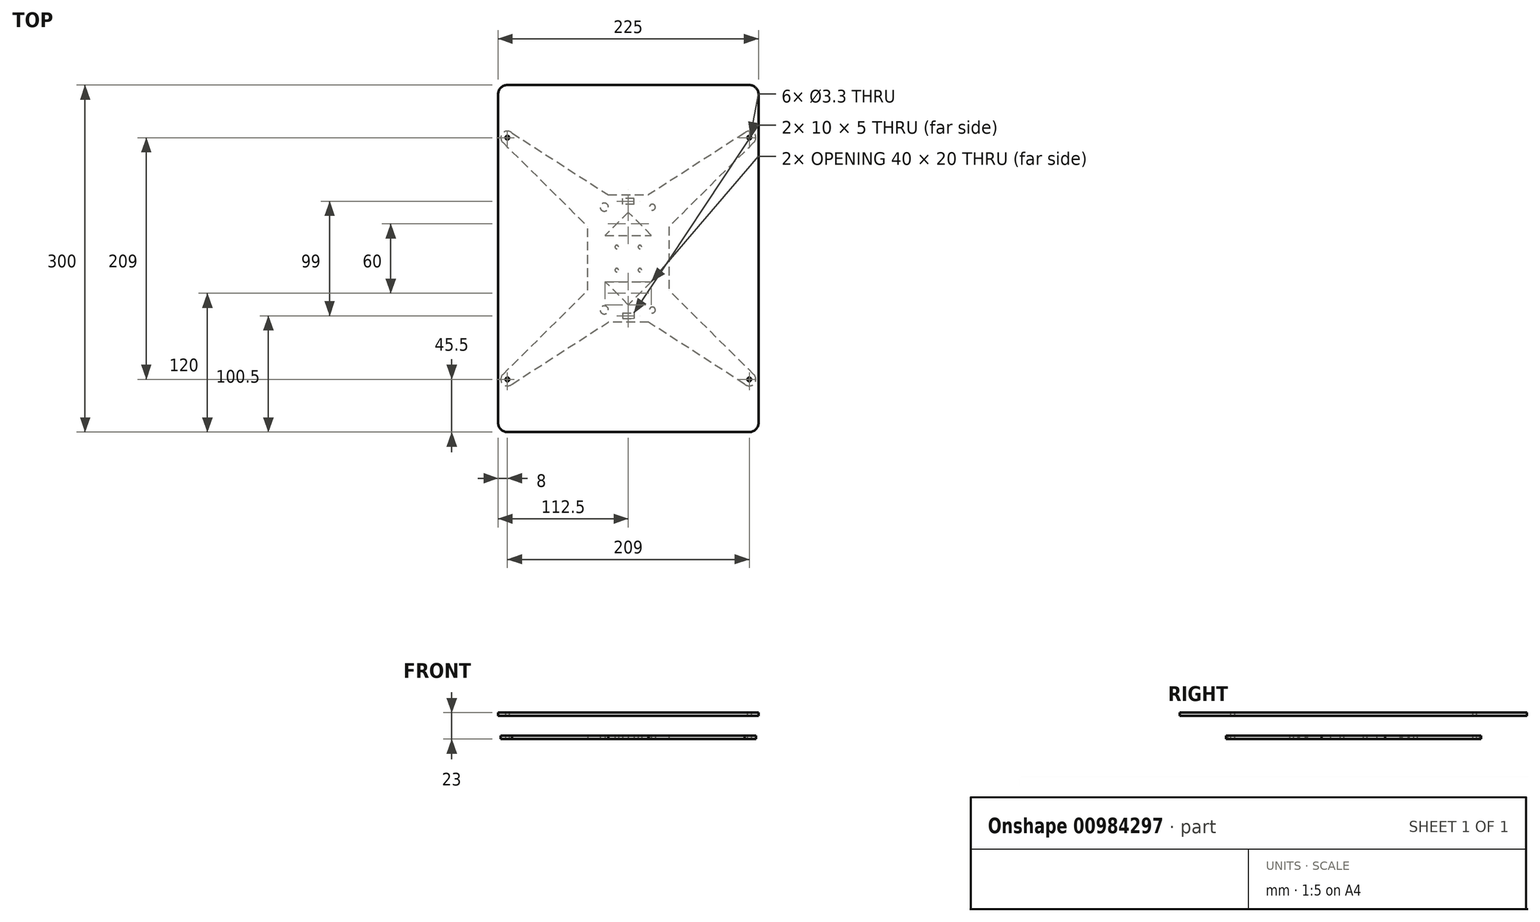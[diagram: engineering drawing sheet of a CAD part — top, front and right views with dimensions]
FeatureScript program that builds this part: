
annotation { "Feature Type Name" : "Feature", "Feature Type Description" : "" }
export const myFeature = defineFeature(function(context is Context, id is Id, definition is map)
    precondition{}
    {
        {
            var Q0;
            Q0=qCreatedBy(makeId("Top.planeOp"),FACE);
            var sketch = newSketch(context, id + "F0", { "sketchPlane" : qUnion([Q0])});
            skCircle(sketch, "E0", {"center": v(-104.5, 104.5) * mm, "radius": 1.65 * mm});
            skArc(sketch, "E1", {"start": v(-100.48, 108.55) * mm, "mid": v(-108.55, 108.52) * mm, "end": v(-108.52, 100.45) * mm});
            skCircle(sketch, "E2.MirrorC", {"center": v(104.5, 104.5) * mm, "radius": 1.65 * mm});
            skArc(sketch, "E3.MirrorCS", {"start": v(100.48, 108.55) * mm, "mid": v(108.55, 108.52) * mm, "end": v(108.52, 100.45) * mm});
            skCircle(sketch, "E4.MirrorC", {"center": v(104.5, -104.5) * mm, "radius": 1.65 * mm});
            skCircle(sketch, "E5.MirrorC", {"center": v(-104.5, -104.5) * mm, "radius": 1.65 * mm});
            skArc(sketch, "E6.MirrorCS", {"start": v(100.48, -108.55) * mm, "mid": v(108.55, -108.52) * mm, "end": v(108.52, -100.45) * mm});
            skArc(sketch, "E7.MirrorCS", {"start": v(-100.48, -108.55) * mm, "mid": v(-108.55, -108.52) * mm, "end": v(-108.52, -100.45) * mm});
            skPoint(sketch, "E8.middle", {"position": v(0, 0) * mm});
            skLineSegment(sketch, "E9", {"start": v(-108.52, 100.45) * mm, "end": v(-35, 27.43) * mm});
            skLineSegment(sketch, "E10", {"start": v(-100.48, 108.55) * mm, "end": v(-17.4, 55) * mm});
            skLineSegment(sketch, "E11", {"start": v(100.48, 108.55) * mm, "end": v(17.4, 55) * mm});
            skLineSegment(sketch, "E12", {"start": v(108.52, 100.45) * mm, "end": v(35, 27.43) * mm});
            skLineSegment(sketch, "E13", {"start": v(-108.52, -100.45) * mm, "end": v(-35, -27.43) * mm});
            skLineSegment(sketch, "E14", {"start": v(-100.48, -108.55) * mm, "end": v(-17.4, -55) * mm});
            skLineSegment(sketch, "E15", {"start": v(100.48, -108.55) * mm, "end": v(17.4, -55) * mm});
            skLineSegment(sketch, "E16", {"start": v(108.52, -100.45) * mm, "end": v(35, -27.43) * mm});
            skLineSegment(sketch, "E17", {"start": v(-17.4, 55) * mm, "end": v(17.4, 55) * mm});
            skLineSegment(sketch, "E18", {"start": v(35, 27.43) * mm, "end": v(35, -27.43) * mm});
            skLineSegment(sketch, "E19", {"start": v(17.4, -55) * mm, "end": v(-17.4, -55) * mm});
            skLineSegment(sketch, "E20", {"start": v(-35, -27.43) * mm, "end": v(-35, 27.43) * mm});
            skLineSegment(sketch, "E21.bottom", {"start": v(5, 47) * mm, "end": v(-5, 47) * mm});
            skLineSegment(sketch, "E21.top", {"start": v(5, 52) * mm, "end": v(-5, 52) * mm});
            skLineSegment(sketch, "E21.left", {"start": v(5, 47) * mm, "end": v(5, 52) * mm});
            skLineSegment(sketch, "E21.right", {"start": v(-5, 47) * mm, "end": v(-5, 52) * mm});
            skPoint(sketch, "E21.middle", {"position": v(0, 49.5) * mm});
            skLineSegment(sketch, "E22.bottom", {"start": v(-5, -47) * mm, "end": v(5, -47) * mm});
            skLineSegment(sketch, "E22.top", {"start": v(-5, -52) * mm, "end": v(5, -52) * mm});
            skLineSegment(sketch, "E22.left", {"start": v(-5, -47) * mm, "end": v(-5, -52) * mm});
            skLineSegment(sketch, "E22.right", {"start": v(5, -47) * mm, "end": v(5, -52) * mm});
            skPoint(sketch, "E22.middle", {"position": v(0, -49.5) * mm});
            skPoint(sketch, "E22.middle.positionSnap0", {"position": v(0, 47) * mm});
            skPoint(sketch, "E22.centerSnap0", {"position": v(0, 47) * mm});
            skCircle(sketch, "E23", {"center": v(-20.8, -44.45) * mm, "radius": 3.56 * mm});
            skCircle(sketch, "E24", {"center": v(20.8, -44.45) * mm, "radius": 2.55 * mm});
            skCircle(sketch, "E25", {"center": v(20.8, 44.45) * mm, "radius": 2.55 * mm});
            skCircle(sketch, "E26", {"center": v(-20.8, 44.45) * mm, "radius": 3.56 * mm});
            skCircle(sketch, "E27", {"center": v(-10, 10) * mm, "radius": 1.5 * mm});
            skCircle(sketch, "E28.MirrorC", {"center": v(10, 10) * mm, "radius": 1.5 * mm});
            skCircle(sketch, "E29.MirrorC", {"center": v(-10, -10) * mm, "radius": 1.5 * mm});
            skCircle(sketch, "E30.MirrorC", {"center": v(10, -10) * mm, "radius": 1.5 * mm});
            skLineSegment(sketch, "E31", {"start": v(0, 40) * mm, "end": v(-20, 20) * mm});
            skLineSegment(sketch, "E32", {"start": v(-20, 20) * mm, "end": v(20, 20) * mm});
            skLineSegment(sketch, "E33", {"start": v(20, 20) * mm, "end": v(0, 40) * mm});
            skLineSegment(sketch, "E34", {"start": v(-20, -20) * mm, "end": v(20, -20) * mm});
            skLineSegment(sketch, "E35", {"start": v(20, -20) * mm, "end": v(0, -40) * mm});
            skLineSegment(sketch, "E36", {"start": v(0, -40) * mm, "end": v(-20, -20) * mm});
            skSolve(sketch);
        }
        {
            var Q0;
            Q0=makeQuery(id+"F0.imprint","IMPRINT",FACE,{"disambiguationData":[TD([[makeQuery(id+"F0.imprint","IMPRINT",EDGE,{"derivedFrom":sQuery(id+"F0.wireOp",EDGE,"E0")}),-1.0]])]});
            var Q1;
            {var subQ1=sQuery(id+"F0.wireOp",EDGE,"E8.bottom");var subQ4=sQuery(id+"F0.wireOp",EDGE,"E8.left");var subQ9=makeQuery(id+"F0.imprint","INTERSECT",VERTEX,{"derivedFrom":[subQ1,subQ4]});Q1=makeQuery(id+"F0.imprint","IMPRINT",FACE,{"disambiguationData":[TD([[makeQuery(id+"F0.imprint","IMPRINT",EDGE,{"disambiguationData":[TD([[subQ9,-1.0]])],"derivedFrom":subQ1}),-1.0]])]});}
            var Q2;
            Q2=makeQuery(id+"F0.imprint","IMPRINT",FACE,{"disambiguationData":[TD([[makeQuery(id+"F0.imprint","IMPRINT",EDGE,{"derivedFrom":sQuery(id+"F0.wireOp",EDGE,"E2.MirrorC")}),1.0]])]});
            var Q3;
            Q3=makeQuery(id+"F0.imprint","IMPRINT",FACE,{"disambiguationData":[TD([[makeQuery(id+"F0.imprint","IMPRINT",EDGE,{"derivedFrom":sQuery(id+"F0.wireOp",EDGE,"E4.MirrorC")}),-1.0]])]});
            var Q4;
            Q4=makeQuery(id+"F0.imprint","IMPRINT",FACE,{"disambiguationData":[TD([[makeQuery(id+"F0.imprint","IMPRINT",EDGE,{"derivedFrom":sQuery(id+"F0.wireOp",EDGE,"E5.MirrorC")}),1.0]])]});
            extrude(context, id + "F1", {"entities" : qUnion([Q0, Q1, Q2, Q3, Q4]), "depth" : 3 * mm, "offsetDistance" : 25 * mm});
        }
        {
            var Q0;
            Q0=qCreatedBy(makeId("Top.planeOp"),FACE);
            var sketch = newSketch(context, id + "F2", { "sketchPlane" : qUnion([Q0])});
            skLineSegment(sketch, "E37.bottom", {"start": v(-104.5, 150) * mm, "end": v(104.5, 150) * mm});
            skLineSegment(sketch, "E37.top", {"start": v(-104.5, -150) * mm, "end": v(104.5, -150) * mm});
            skLineSegment(sketch, "E37.left", {"start": v(-112.5, 142) * mm, "end": v(-112.5, -142) * mm});
            skLineSegment(sketch, "E37.right", {"start": v(112.5, 142) * mm, "end": v(112.5, -142) * mm});
            skPoint(sketch, "E37.middle", {"position": v(0, 0) * mm});
            skPoint(sketch, "E38.visualSharp", {"position": v(-112.5, 150) * mm});
            skArc(sketch, "E38.filletArc", {"start": v(-104.5, 150) * mm, "mid": v(-110.16, 147.66) * mm, "end": v(-112.5, 142) * mm});
            skPoint(sketch, "E39.visualSharp", {"position": v(112.5, 150) * mm});
            skArc(sketch, "E39.filletArc", {"start": v(112.5, 142) * mm, "mid": v(110.16, 147.66) * mm, "end": v(104.5, 150) * mm});
            skPoint(sketch, "E40.visualSharp", {"position": v(112.5, -150) * mm});
            skArc(sketch, "E40.filletArc", {"start": v(104.5, -150) * mm, "mid": v(110.16, -147.66) * mm, "end": v(112.5, -142) * mm});
            skPoint(sketch, "E41.visualSharp", {"position": v(-112.5, -150) * mm});
            skArc(sketch, "E41.filletArc", {"start": v(-112.5, -142) * mm, "mid": v(-110.16, -147.66) * mm, "end": v(-104.5, -150) * mm});
            skCircle(sketch, "E42", {"center": v(-104.5, 104.5) * mm, "radius": 1.65 * mm});
            skCircle(sketch, "E43", {"center": v(104.5, 104.5) * mm, "radius": 1.65 * mm});
            skCircle(sketch, "E44", {"center": v(104.5, -104.5) * mm, "radius": 1.65 * mm});
            skCircle(sketch, "E45", {"center": v(-104.5, -104.5) * mm, "radius": 1.65 * mm});
            skSolve(sketch);
        }
        {
            var Q0;
            Q0=makeQuery(id+"F2.imprint","IMPRINT",FACE,{"disambiguationData":[TD([[makeQuery(id+"F2.imprint","IMPRINT",EDGE,{"derivedFrom":sQuery(id+"F2.wireOp",EDGE,"E37.bottom")}),-1.0]])]});
            extrude(context, id + "F3", {"entities" : qUnion([Q0]), "depth" : 23 * mm, "offsetDistance" : 25 * mm, "hasSecondDirection" : true, "secondDirectionOppositeDirection" : false, "secondDirectionDepth" : 20 * mm});
        }
    });
